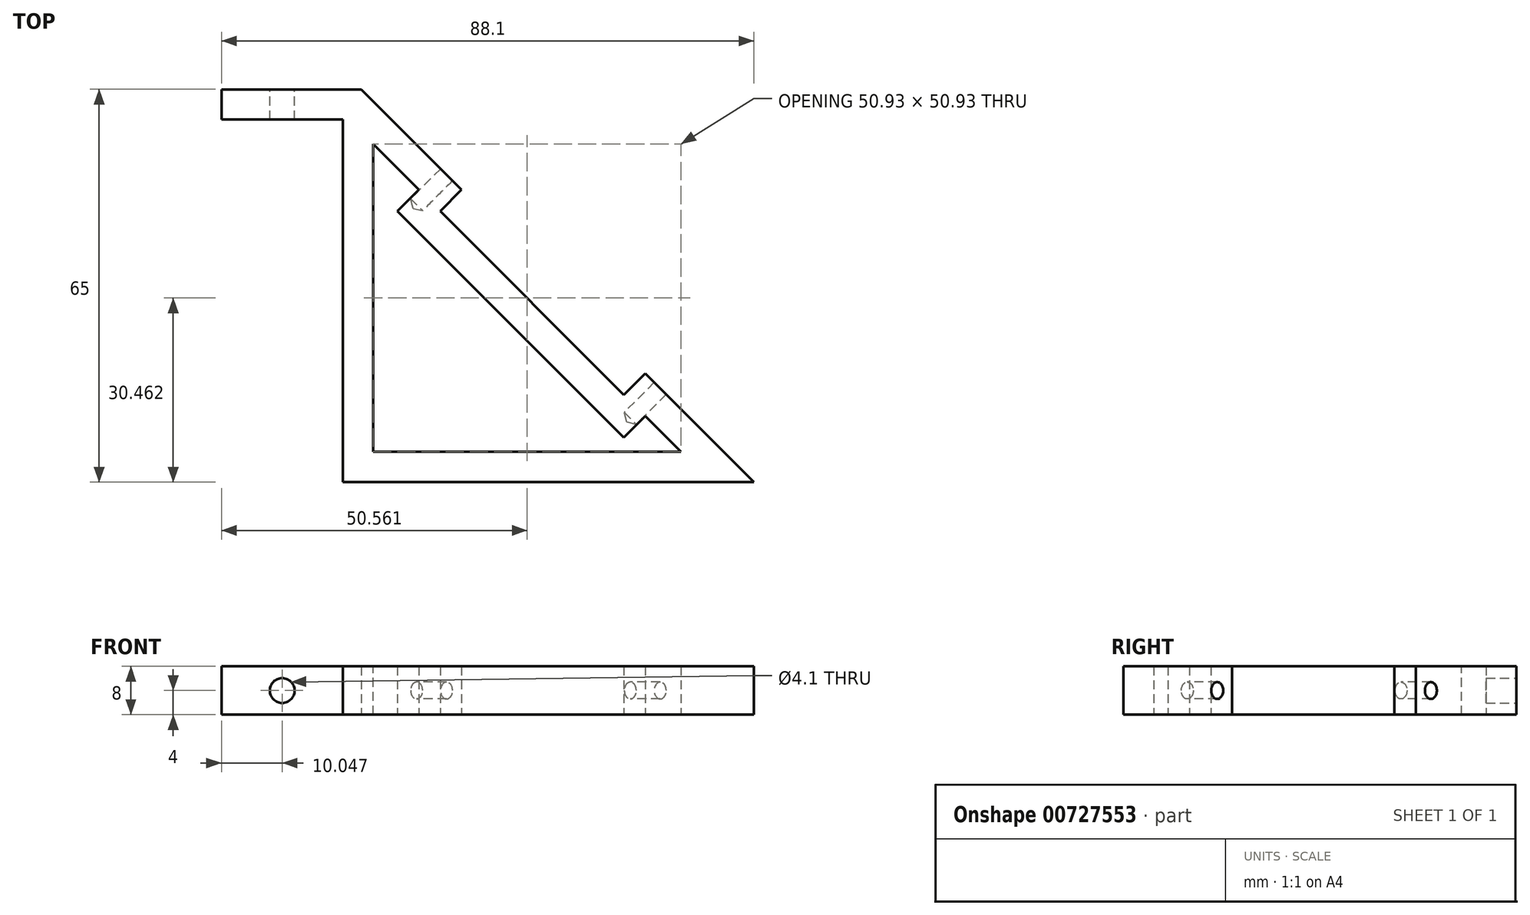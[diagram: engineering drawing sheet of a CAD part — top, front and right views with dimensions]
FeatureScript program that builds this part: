
annotation { "Feature Type Name" : "Feature", "Feature Type Description" : "" }
export const myFeature = defineFeature(function(context is Context, id is Id, definition is map)
    precondition{}
    {
        {
            var Q0;
            Q0=qCreatedBy(makeId("Top.planeOp"),FACE);
            var sketch = newSketch(context, id + "F0", { "sketchPlane" : qUnion([Q0])});
            skLineSegment(sketch, "E0", {"start": v(-0.87, 11.74) * mm, "end": v(22.23, 11.74) * mm});
            skLineSegment(sketch, "E1", {"start": v(22.23, 11.74) * mm, "end": v(87.23, -53.26) * mm});
            skLineSegment(sketch, "E2", {"start": v(87.23, -53.26) * mm, "end": v(19.23, -53.26) * mm});
            skLineSegment(sketch, "E3", {"start": v(19.23, -53.26) * mm, "end": v(19.23, 6.74) * mm});
            skLineSegment(sketch, "E4", {"start": v(19.23, 6.74) * mm, "end": v(-0.87, 6.74) * mm});
            skLineSegment(sketch, "E5", {"start": v(-0.87, 6.74) * mm, "end": v(-0.87, 11.74) * mm});
            skSolve(sketch);
        }
        {
            var Q0;
            Q0=makeQuery(id+"F0.imprint","IMPRINT",FACE,{"disambiguationData":[TD([[makeQuery(id+"F0.imprint","IMPRINT",EDGE,{"derivedFrom":sQuery(id+"F0.wireOp",EDGE,"E0")}),-1.0]])]});
            extrude(context, id + "F1", {"entities" : qUnion([Q0]), "depth" : 8 * mm, "offsetDistance" : 25 * mm});
        }
        {
            var Q0;
            Q0=makeQuery(id+"F1.opExtrude","SWEPT_FACE",FACE,{"disambiguationData":[OSD([sQuery(id+"F0.wireOp",EDGE,"E4")])]});
            var sketch = newSketch(context, id + "F2", { "sketchPlane" : qUnion([Q0])});
            skLineSegment(sketch, "E6", {"start": v(-0.87, 8) * mm, "end": v(19.23, 0) * mm, "construction": true});
            skPoint(sketch, "E7", {"position": v(9.18, 4) * mm});
            skSolve(sketch);
        }
        {
            var Q0;
            Q0=sQuery(id+"F2.wireOp",VERTEX,"E7");
            var Q1;
            Q1=makeQuery(id+"F1.opExtrude","SWEPT_BODY",BODY,{"disambiguationData":[OSD([sQuery(id+"F0.wireOp",EDGE,"E0"),sQuery(id+"F0.wireOp",EDGE,"E1"),sQuery(id+"F0.wireOp",EDGE,"E2"),sQuery(id+"F0.wireOp",EDGE,"E3"),sQuery(id+"F0.wireOp",EDGE,"E4"),sQuery(id+"F0.wireOp",EDGE,"E5")])]});
            hole(context, id + "F3", {"style" : HoleStyle.SIMPLE, "endStyle" : HoleEndStyle.BLIND, "holeDiameter" : 4.1 * mm, "majorDiameter" : 5 * mm, "holeDepth" : 7 * mm, "tappedDepth" : 30 * mm, "tapClearance" : 3, "startFromSketch" : true, "locations" : qUnion([Q0]), "scope" : qUnion([Q1])});
        }
        {
            var Q0;
            Q0=makeQuery(id+"F1.opExtrude","SWEPT_FACE",FACE,{"disambiguationData":[OSD([sQuery(id+"F0.wireOp",EDGE,"E1")])]});
            var sketch = newSketch(context, id + "F4", { "sketchPlane" : qUnion([Q0])});
            skLineSegment(sketch, "E8", {"start": v(-7.42, 4) * mm, "end": v(-99.34, 4) * mm, "construction": true});
            skPoint(sketch, "E9", {"position": v(-27.42, 4) * mm});
            skPoint(sketch, "E10", {"position": v(-77.42, 4) * mm});
            skLineSegment(sketch, "E11.bottom", {"start": v(-30.92, 8) * mm, "end": v(-73.92, 8) * mm});
            skLineSegment(sketch, "E11.top", {"start": v(-30.92, 0) * mm, "end": v(-73.92, 0) * mm});
            skLineSegment(sketch, "E11.left", {"start": v(-30.92, 8) * mm, "end": v(-30.92, 0) * mm});
            skLineSegment(sketch, "E11.right", {"start": v(-73.92, 8) * mm, "end": v(-73.92, 0) * mm});
            skSolve(sketch);
        }
        {
            var Q0;
            Q0 = qSketchRegion(id + "F4", true);
            extrude(context, id + "F5", {"entities" : qUnion([Q0]), "operationType" : NewBodyOperationType.REMOVE, "oppositeDirection" : true, "depth" : 5 * mm, "offsetDistance" : 25 * mm});
        }
        {
            var Q0;
            Q0=makeQuery(id+"F1.opExtrude","CAP_FACE",FACE,{"disambiguationData":[OSD([sQuery(id+"F0.wireOp",EDGE,"E0"),sQuery(id+"F0.wireOp",EDGE,"E1"),sQuery(id+"F0.wireOp",EDGE,"E2"),sQuery(id+"F0.wireOp",EDGE,"E3"),sQuery(id+"F0.wireOp",EDGE,"E4"),sQuery(id+"F0.wireOp",EDGE,"E5")])],"isStart":false});
            var Q1;
            Q1=makeQuery(id+"F1.opExtrude","CAP_FACE",FACE,{"disambiguationData":[OSD([sQuery(id+"F0.wireOp",EDGE,"E0"),sQuery(id+"F0.wireOp",EDGE,"E1"),sQuery(id+"F0.wireOp",EDGE,"E2"),sQuery(id+"F0.wireOp",EDGE,"E3"),sQuery(id+"F0.wireOp",EDGE,"E4"),sQuery(id+"F0.wireOp",EDGE,"E5")])],"isStart":true});
            shell(context, id + "F6", {"entities" : qUnion([Q0, Q1]), "thickness" : 5 * mm});
        }
        {
            var Q0;
            Q0=sQuery(id+"F4.wireOp",VERTEX,"E9");
            var Q1;
            Q1=sQuery(id+"F4.wireOp",VERTEX,"E10");
            var Q2;
            Q2=makeQuery(id+"F1.opExtrude","SWEPT_BODY",BODY,{"disambiguationData":[OSD([sQuery(id+"F0.wireOp",EDGE,"E0"),sQuery(id+"F0.wireOp",EDGE,"E1"),sQuery(id+"F0.wireOp",EDGE,"E2"),sQuery(id+"F0.wireOp",EDGE,"E3"),sQuery(id+"F0.wireOp",EDGE,"E4"),sQuery(id+"F0.wireOp",EDGE,"E5")])]});
            hole(context, id + "F7", {"style" : HoleStyle.SIMPLE, "endStyle" : HoleEndStyle.BLIND, "holeDiameter" : 2.8 * mm, "majorDiameter" : 5 * mm, "holeDepth" : 7 * mm, "tappedDepth" : 30 * mm, "tapClearance" : 3, "startFromSketch" : true, "locations" : qUnion([Q0, Q1]), "scope" : qUnion([Q2])});
        }
    });
